# Revit family: КСА_Eng
name_source: partatom
category: Mechanical Equipment
units: mm (PartAtom-declared; Revit-internal decimal feet)

## family parameters
Always vertical = Yes
Classification = None
Cut with Voids When Loaded = No
Part Type = Normal
Room Calculation Point = No
Round Connector Dimension = Use Diameter
Shared = No
Work Plane-Based = No

## types (5) — shared parameters
00_20_Manufacturer = Vents
00_20_Name = Centrifugal fan
Casing Material = Steel, galvanized
Description = Heat-and sound-insulated casing
Frequency = 50 Hz
Load Classification = HVAC
Maintenance zone material = <By Category>
Manufacturer = Vents
Number of Fase = 1
P = 48 mm  [stored 0.15748 ft]
Temperature of moving air = -25...+40 °C
URL = https://ventilation-system.com
Voltage = 230 V
zero-valued in all types: Default Elevation

## per-type parameters (varying)
| type | Amperage | Apparent Load | B | D | Diameter | Dy | H | H1 | Height | L | Length | Maximum Air Flow | Power | Sound pressure level at 3 m distance | Weight | Width | b | b1 | h | l | l1 |
| KSA 100-2E | 1 A | 138 VA | 184 mm  [stored 0.603675 ft] | 100 mm  [stored 0.328084 ft] | 100 mm  [stored 0.328084 ft] | 95 mm  [stored 0.31168 ft] | 308 mm  [stored 1.0105 ft] | 260 mm  [stored 0.853018 ft] | 308 mm  [stored 1.0105 ft] | 310 mm  [stored 1.01706 ft] | 310 mm  [stored 1.01706 ft] | 425.0 m³/h | 130 W | 36.1 dBA | 4.22 kg | 184 mm  [stored 0.603675 ft] | 136 mm | 140 mm  [stored 0.459318 ft] | 103 mm | 103 mm | 70 mm  [stored 0.229659 ft] |
| KSA 200-4E | 1 A | 115 VA | 282 mm | 200 mm  [stored 0.656168 ft] | 200 mm  [stored 0.656168 ft] | 195 mm  [stored 0.639764 ft] | 408 mm | 360 mm | 408 mm | 445 mm  [stored 1.45997 ft] | 445 mm  [stored 1.45997 ft] | 640.0 m³/h | 115 W | 29.1 dBA | 8.25 kg | 282 mm | 234 mm  [stored 0.767717 ft] | 238 mm  [stored 0.78084 ft] | 136 mm | 148 mm | 120 mm  [stored 0.393701 ft] |
| KSA 125-2E | 1 A | 161 VA | 204 mm | 125 mm  [stored 0.410105 ft] | 125 mm  [stored 0.410105 ft] | 120 mm  [stored 0.393701 ft] | 308 mm  [stored 1.0105 ft] | 260 mm  [stored 0.853018 ft] | 308 mm  [stored 1.0105 ft] | 310 mm  [stored 1.01706 ft] | 310 mm  [stored 1.01706 ft] | 505.0 m³/h | 155 W | 38.3 dBA | 4.57 kg | 204 mm | 156 mm  [stored 0.511811 ft] | 160 mm  [stored 0.524934 ft] | 103 mm | 103 mm | 83 mm |
| KSA 150-2E | 2 A | 345 VA | 231 mm  [stored 0.757874 ft] | 150 mm | 150 mm | 145 mm  [stored 0.475722 ft] | 343 mm  [stored 1.12533 ft] | 295 mm  [stored 0.967848 ft] | 343 mm  [stored 1.12533 ft] | 358 mm  [stored 1.17454 ft] | 358 mm  [stored 1.17454 ft] | 750.0 m³/h | 335 W | 39.4 dBA | 6.28 kg | 231 mm  [stored 0.757874 ft] | 183 mm | 187 mm  [stored 0.613517 ft] | 114 mm | 119 mm | 95 mm  [stored 0.31168 ft] |
| KSA 160-2E | 2 A | 345 VA | 231 mm  [stored 0.757874 ft] | 160 mm  [stored 0.524934 ft] | 160 mm  [stored 0.524934 ft] | 155 mm  [stored 0.50853 ft] | 343 mm  [stored 1.12533 ft] | 295 mm  [stored 0.967848 ft] | 343 mm  [stored 1.12533 ft] | 358 mm  [stored 1.17454 ft] | 358 mm  [stored 1.17454 ft] | 750.0 m³/h | 335 W | 37.9 dBA | 6.28 kg | 231 mm  [stored 0.757874 ft] | 183 mm | 187 mm  [stored 0.613517 ft] | 114 mm | 119 mm | 100 mm  [stored 0.328084 ft] |

note: column(s) folded — value = type name in every type: 00_20_Type

note: [stored X ft] marks values corroborated as IEEE doubles in the binary element streams (Revit-internal decimal feet)
